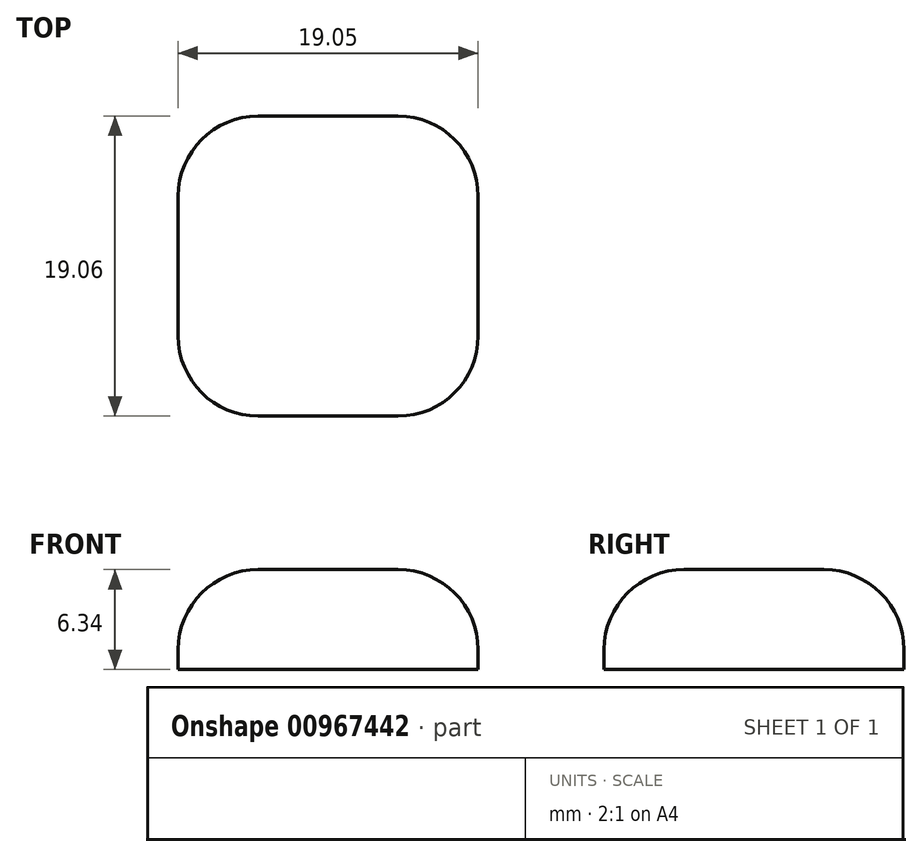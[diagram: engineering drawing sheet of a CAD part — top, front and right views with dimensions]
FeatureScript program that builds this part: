
annotation { "Feature Type Name" : "Feature", "Feature Type Description" : "" }
export const myFeature = defineFeature(function(context is Context, id is Id, definition is map)
    precondition{}
    {
        {
            var Q0;
            Q0=qCreatedBy(makeId("Top.planeOp"),FACE);
            var sketch = newSketch(context, id + "F0", { "sketchPlane" : qUnion([Q0])});
            skLineSegment(sketch, "E0.bottom", {"start": v(5.4, -9.53) * mm, "end": v(-13.65, -9.53) * mm});
            skLineSegment(sketch, "E0.top", {"start": v(5.4, 9.53) * mm, "end": v(-13.65, 9.53) * mm});
            skLineSegment(sketch, "E0.left", {"start": v(5.4, -9.53) * mm, "end": v(5.4, 9.53) * mm});
            skLineSegment(sketch, "E0.right", {"start": v(-13.65, -9.53) * mm, "end": v(-13.65, 9.53) * mm});
            skPoint(sketch, "E0.middle", {"position": v(-4.12, 0) * mm});
            skSolve(sketch);
        }
        {
            var Q0;
            Q0=qSketchRegion(id+"F0",true);
            extrude(context, id + "F1", {"entities" : qUnion([Q0]), "endBound" : BoundingType.SYMMETRIC, "depth" : 6.35 * mm});
        }
        {
            var Q0;
            Q0=makeQuery(id+"F1.opExtrude","CAP_FACE",FACE,{"disambiguationData":[OSD([sQuery(id+"F0.wireOp",EDGE,"E0.bottom"),sQuery(id+"F0.wireOp",EDGE,"E0.top"),sQuery(id+"F0.wireOp",EDGE,"E0.left"),sQuery(id+"F0.wireOp",EDGE,"E0.right")])],"isStart":false});
            var Q1;
            Q1=makeQuery(id+"F1.opExtrude","SWEPT_EDGE",EDGE,{"disambiguationData":[OSD([sQuery(id+"F0.wireOp",EDGE,"E0.bottom"),sQuery(id+"F0.wireOp",EDGE,"E0.left")])]});
            var Q2;
            Q2=makeQuery(id+"F1.opExtrude","SWEPT_EDGE",EDGE,{"disambiguationData":[OSD([sQuery(id+"F0.wireOp",EDGE,"E0.bottom"),sQuery(id+"F0.wireOp",EDGE,"E0.right")])]});
            var Q3;
            Q3=makeQuery(id+"F1.opExtrude","SWEPT_EDGE",EDGE,{"disambiguationData":[OSD([sQuery(id+"F0.wireOp",EDGE,"E0.top"),sQuery(id+"F0.wireOp",EDGE,"E0.right")])]});
            var Q4;
            Q4=makeQuery(id+"F1.opExtrude","SWEPT_EDGE",EDGE,{"disambiguationData":[OSD([sQuery(id+"F0.wireOp",EDGE,"E0.top"),sQuery(id+"F0.wireOp",EDGE,"E0.left")])]});
            fillet(context, id + "F2", {"entities" : qUnion([Q0, Q1, Q2, Q3, Q4]), "radius" : 5.08 * mm, "tangentPropagation" : true, "allowEdgeOverflow" : false});
        }
    });
